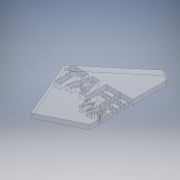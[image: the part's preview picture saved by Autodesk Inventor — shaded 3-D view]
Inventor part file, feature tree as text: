
AUTODESK INVENTOR PART (.ipt)
format: ipt  version: 2018 (Build 220112000, 112)  size: 219,136 bytes
history: native  units: mm
features: sketch x2, extrude x2
ambient origin geometry x8: Origin, YZ Plane, XZ Plane, XY Plane, X Axis, Y Axis, Z Axis, Center Point
bodies: Solid1 (feature_tree)
feature tree (4):
  sketch  "Sketch1"  dims[d39=3.0mm d41=12.0mm]
  sketch  "Sketch2"  dims[d44=2.5mm d45=2.5mm d46=3.0mm d47=5.3mm d48=5.0mm d49=3.0mm d50=3.3mm d51=3.0mm d52=3.0mm d55=5.9mm d56=75.0deg d57=6.0mm d58=75.0deg d62=6.981317mm d69=21.816616mm d70=20.257173mm d71=8.726646mm d72=4.014257mm d73=18.58376mm d74=45.750155mm d75=13.725103mm d76=28.308135mm d77=13.269457mm d78=3.0mm d79=0.0mm d80=3.0mm d81=0.0mm]
  extrude  "Extrusion1"  Depth=3.0mm
  extrude  "Extrusion2"  Depth=3.0mm
